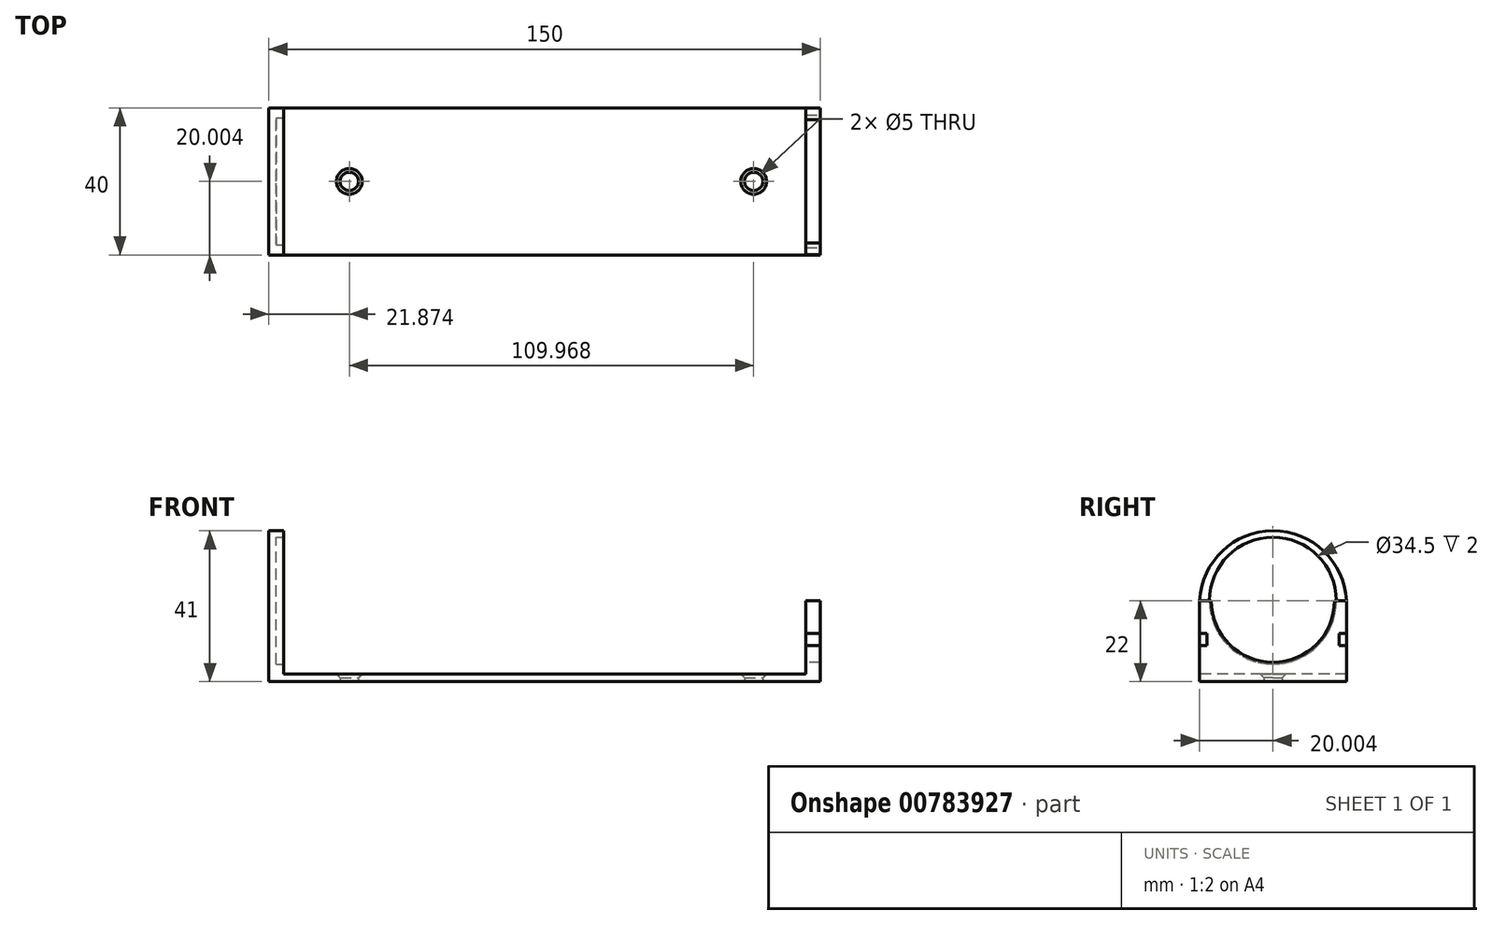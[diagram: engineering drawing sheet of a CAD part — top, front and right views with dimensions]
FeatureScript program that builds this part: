
annotation { "Feature Type Name" : "Feature", "Feature Type Description" : "" }
export const myFeature = defineFeature(function(context is Context, id is Id, definition is map)
    precondition{}
    {
        {
            var Q0;
            Q0=qCreatedBy(makeId("Top.planeOp"),FACE);
            var sketch = newSketch(context, id + "F0", { "sketchPlane" : qUnion([Q0])});
            skLineSegment(sketch, "E0.bottom", {"start": v(-45.04, -26.37) * mm, "end": v(104.96, -26.37) * mm});
            skLineSegment(sketch, "E0.top", {"start": v(-45.04, 13.63) * mm, "end": v(104.96, 13.63) * mm});
            skLineSegment(sketch, "E0.left", {"start": v(-45.04, -26.37) * mm, "end": v(-45.04, 13.63) * mm});
            skLineSegment(sketch, "E0.right", {"start": v(104.96, -26.37) * mm, "end": v(104.96, 13.63) * mm});
            skSolve(sketch);
        }
        {
            var Q0;
            Q0=makeQuery(id+"F0.imprint","IMPRINT",FACE,{"disambiguationData":[TD([[makeQuery(id+"F0.imprint","IMPRINT",EDGE,{"derivedFrom":sQuery(id+"F0.wireOp",EDGE,"E0.bottom")}),1.0]])]});
            extrude(context, id + "F1", {"entities" : qUnion([Q0]), "depth" : 2 * mm, "offsetDistance" : 25 * mm});
        }
        {
            var Q0;
            Q0=makeQuery(id+"F1.opExtrude","CAP_FACE",FACE,{"disambiguationData":[OSD([sQuery(id+"F0.wireOp",EDGE,"E0.bottom"),sQuery(id+"F0.wireOp",EDGE,"E0.top"),sQuery(id+"F0.wireOp",EDGE,"E0.left"),sQuery(id+"F0.wireOp",EDGE,"E0.right")])],"isStart":false});
            var sketch = newSketch(context, id + "F2", { "sketchPlane" : qUnion([Q0])});
            skLineSegment(sketch, "E1.bottom", {"start": v(-45.04, 13.63) * mm, "end": v(-41.04, 13.63) * mm});
            skLineSegment(sketch, "E1.top", {"start": v(-45.04, -26.37) * mm, "end": v(-41.04, -26.37) * mm});
            skLineSegment(sketch, "E1.left", {"start": v(-45.04, 13.63) * mm, "end": v(-45.04, -26.37) * mm});
            skLineSegment(sketch, "E1.right", {"start": v(-41.04, 13.63) * mm, "end": v(-41.04, -26.37) * mm});
            skLineSegment(sketch, "E2.bottom", {"start": v(104.96, 13.63) * mm, "end": v(102.96, 13.63) * mm});
            skLineSegment(sketch, "E2.top", {"start": v(104.96, -26.37) * mm, "end": v(102.96, -26.37) * mm});
            skLineSegment(sketch, "E2.left", {"start": v(104.96, 13.63) * mm, "end": v(104.96, -26.37) * mm});
            skLineSegment(sketch, "E2.right", {"start": v(102.96, 13.63) * mm, "end": v(102.96, -26.37) * mm});
            skSolve(sketch);
        }
        {
            var Q0;
            Q0=makeQuery(id+"F2.imprint","IMPRINT",FACE,{"disambiguationData":[TD([[makeQuery(id+"F2.imprint","IMPRINT",EDGE,{"derivedFrom":sQuery(id+"F2.wireOp",EDGE,"E1.bottom")}),-1.0]])]});
            var Q1;
            Q1=makeQuery(id+"F2.imprint","IMPRINT",FACE,{"disambiguationData":[TD([[makeQuery(id+"F2.imprint","IMPRINT",EDGE,{"derivedFrom":sQuery(id+"F2.wireOp",EDGE,"E2.bottom")}),-1.0]])]});
            extrude(context, id + "F3", {"entities" : qUnion([Q0, Q1]), "operationType" : NewBodyOperationType.ADD, "depth" : 40 * mm, "offsetDistance" : 25 * mm});
        }
        {
            var Q0;
            Q0=makeQuery(id+"F3.opExtrude","SWEPT_FACE",FACE,{"disambiguationData":[OSD([sQuery(id+"F2.wireOp",EDGE,"E1.right")])]});
            var sketch = newSketch(context, id + "F4", { "sketchPlane" : qUnion([Q0])});
            skCircle(sketch, "E3", {"center": v(-6.37, 22) * mm, "radius": 17.25 * mm});
            skSolve(sketch);
        }
        {
            var Q0;
            Q0=makeQuery(id+"F4.imprint","IMPRINT",FACE,{"disambiguationData":[TD([[makeQuery(id+"F4.imprint","IMPRINT",EDGE,{"derivedFrom":sQuery(id+"F4.wireOp",EDGE,"E3")}),1.0]])]});
            var Q1;
            Q1=sQuery(id+"F4.wireOp",EDGE,"E3");
            extrude(context, id + "F5", {"entities" : qUnion([Q0]), "operationType" : NewBodyOperationType.REMOVE, "surfaceEntities" : qUnion([Q1]), "oppositeDirection" : true, "depth" : 2 * mm, "offsetDistance" : 25 * mm});
        }
        {
            var Q0;
            Q0=makeQuery(id+"F3.opExtrude","SWEPT_FACE",FACE,{"disambiguationData":[OSD([sQuery(id+"F2.wireOp",EDGE,"E2.right")])]});
            var sketch = newSketch(context, id + "F6", { "sketchPlane" : qUnion([Q0])});
            skLineSegment(sketch, "E4", {"start": v(-10.38, 22) * mm, "end": v(23.12, 22) * mm});
            skArc(sketch, "E5", {"start": v(-10.38, 22) * mm, "mid": v(6.37, 5.25) * mm, "end": v(23.12, 22) * mm});
            skPoint(sketch, "E6.orphan", {"position": v(-13.63, 22) * mm});
            skPoint(sketch, "E7.orphan", {"position": v(26.37, 22) * mm});
            skSolve(sketch);
        }
        {
            var Q0;
            Q0=makeQuery(id+"F3.opExtrude","CAP_FACE",FACE,{"disambiguationData":[OSD([sQuery(id+"F2.wireOp",EDGE,"E2.bottom"),sQuery(id+"F2.wireOp",EDGE,"E2.top"),sQuery(id+"F2.wireOp",EDGE,"E2.left"),sQuery(id+"F2.wireOp",EDGE,"E2.right")])],"isStart":false});
            extrude(context, id + "F7", {"entities" : qUnion([Q0]), "operationType" : NewBodyOperationType.REMOVE, "oppositeDirection" : true, "depth" : 20 * mm, "offsetDistance" : 25 * mm});
        }
        {
            var Q0;
            Q0=makeQuery(id+"F6.imprint","IMPRINT",FACE,{"disambiguationData":[TD([[makeQuery(id+"F6.imprint","IMPRINT",EDGE,{"derivedFrom":sQuery(id+"F6.wireOp",EDGE,"E4")}),-1.0]])]});
            extrude(context, id + "F8", {"entities" : qUnion([Q0]), "operationType" : NewBodyOperationType.REMOVE, "endBound" : BoundingType.THROUGH_ALL, "oppositeDirection" : true, "depth" : 25 * mm, "offsetDistance" : 25 * mm});
        }
        {
            var Q0;
            Q0=makeQuery(id+"F1.opExtrude","CAP_FACE",FACE,{"disambiguationData":[OSD([sQuery(id+"F0.wireOp",EDGE,"E0.bottom"),sQuery(id+"F0.wireOp",EDGE,"E0.top"),sQuery(id+"F0.wireOp",EDGE,"E0.left"),sQuery(id+"F0.wireOp",EDGE,"E0.right")])],"isStart":true});
            var sketch = newSketch(context, id + "F9", { "sketchPlane" : qUnion([Q0])});
            skCircle(sketch, "E8", {"center": v(86.8, 6.37) * mm, "radius": 2.5 * mm});
            skCircle(sketch, "E9", {"center": v(-23.17, 6.37) * mm, "radius": 2.5 * mm});
            skSolve(sketch);
        }
        {
            var Q0;
            Q0=makeQuery(id+"F9.imprint","IMPRINT",FACE,{"disambiguationData":[TD([[makeQuery(id+"F9.imprint","IMPRINT",EDGE,{"derivedFrom":sQuery(id+"F9.wireOp",EDGE,"E9")}),1.0]])]});
            var Q1;
            Q1=makeQuery(id+"F9.imprint","IMPRINT",FACE,{"disambiguationData":[TD([[makeQuery(id+"F9.imprint","IMPRINT",EDGE,{"derivedFrom":sQuery(id+"F9.wireOp",EDGE,"E8")}),1.0]])]});
            extrude(context, id + "F10", {"entities" : qUnion([Q0, Q1]), "operationType" : NewBodyOperationType.REMOVE, "endBound" : BoundingType.THROUGH_ALL, "oppositeDirection" : true, "depth" : 25 * mm, "offsetDistance" : 25 * mm});
        }
        {
            var Q0;
            Q0=makeQuery(id+"F3.boolean.opBoolean","MERGE",FACE,{"derivedFrom":[makeQuery(id+"F1.opExtrude","SWEPT_FACE",FACE,{"disambiguationData":[OSD([sQuery(id+"F0.wireOp",EDGE,"E0.right")])]}),makeQuery(id+"F3.opExtrude","SWEPT_FACE",FACE,{"disambiguationData":[OSD([sQuery(id+"F2.wireOp",EDGE,"E2.left")])]})]});
            var sketch = newSketch(context, id + "F11", { "sketchPlane" : qUnion([Q0])});
            skLineSegment(sketch, "E10", {"start": v(-26.37, 13.12) * mm, "end": v(-24.37, 13.12) * mm});
            skLineSegment(sketch, "E11", {"start": v(-26.37, 9.8) * mm, "end": v(-24.37, 9.8) * mm});
            skLineSegment(sketch, "E12.0", {"start": v(-24.37, 13.12) * mm, "end": v(-24.37, 9.8) * mm});
            skLineSegment(sketch, "E13.0", {"start": v(11.63, 13.12) * mm, "end": v(11.63, 9.8) * mm});
            skLineSegment(sketch, "E14.trimOffspring", {"start": v(11.63, 13.12) * mm, "end": v(13.63, 13.12) * mm});
            skLineSegment(sketch, "E15.trimOffspring", {"start": v(11.63, 9.8) * mm, "end": v(13.63, 9.8) * mm});
            skSolve(sketch);
        }
        {
            var Q0;
            {var subQ0=sQuery(id+"F11.wireOp",EDGE,"E10");Q0=makeQuery(id+"F11.imprint","IMPRINT",FACE,{"disambiguationData":[TD([[makeQuery(id+"F11.imprint","IMPRINT",EDGE,{"derivedFrom":subQ0}),-1.0]])]});}
            var Q1;
            Q1=makeQuery(id+"F11.imprint","IMPRINT",FACE,{"disambiguationData":[TD([[makeQuery(id+"F11.imprint","IMPRINT",EDGE,{"derivedFrom":sQuery(id+"F11.wireOp",EDGE,"E13.0")}),1.0]])]});
            extrude(context, id + "F12", {"entities" : qUnion([Q0, Q1]), "operationType" : NewBodyOperationType.REMOVE, "oppositeDirection" : true, "depth" : 25 * mm, "offsetDistance" : 25 * mm});
        }
        {
            var Q0;
            Q0=makeQuery(id+"F3.boolean.opBoolean","MERGE",FACE,{"derivedFrom":[makeQuery(id+"F1.opExtrude","SWEPT_FACE",FACE,{"disambiguationData":[OSD([sQuery(id+"F0.wireOp",EDGE,"E0.left")])]}),makeQuery(id+"F3.opExtrude","SWEPT_FACE",FACE,{"disambiguationData":[OSD([sQuery(id+"F2.wireOp",EDGE,"E1.left")])]})]});
            var sketch = newSketch(context, id + "F13", { "sketchPlane" : qUnion([Q0])});
            skCircle(sketch, "E16", {"center": v(6.37, 21) * mm, "radius": 20 * mm});
            skPoint(sketch, "E16.centerSnap0", {"position": v(-13.63, 21) * mm});
            skPoint(sketch, "E16.centerSnap1", {"position": v(6.37, 42) * mm});
            skSolve(sketch);
        }
        {
            var Q0;
            {var subQ1=sQuery(id+"F2.wireOp",EDGE,"E1.left");var subQ7=makeQuery(id+"F3.opExtrude","CAP_EDGE",EDGE,{"disambiguationData":[OSD([subQ1])],"isStart":false});Q0=makeQuery(id+"F13.imprint","IMPRINT",FACE,{"disambiguationData":[TD([[makeQuery(id+"F13.imprint","IMPRINT",EDGE,{"derivedFrom":subQ7}),1.0]])]});}
            extrude(context, id + "F14", {"entities" : qUnion([Q0]), "operationType" : NewBodyOperationType.REMOVE, "endBound" : BoundingType.THROUGH_ALL, "oppositeDirection" : true, "depth" : 25 * mm, "offsetDistance" : 25 * mm});
        }
        {
            var Q0;
            Q0=makeQuery(id+"F10.boolean.opBoolean","INTERSECT",EDGE,{"derivedFrom":[makeQuery(id+"F1.opExtrude","CAP_FACE",FACE,{"disambiguationData":[OSD([sQuery(id+"F0.wireOp",EDGE,"E0.bottom"),sQuery(id+"F0.wireOp",EDGE,"E0.top"),sQuery(id+"F0.wireOp",EDGE,"E0.left"),sQuery(id+"F0.wireOp",EDGE,"E0.right")])],"isStart":false}),makeQuery(id+"F10.opExtrude","SWEPT_FACE",FACE,{"disambiguationData":[OSD([sQuery(id+"F9.wireOp",EDGE,"E9")])]})]});
            var Q1;
            Q1=makeQuery(id+"F10.boolean.opBoolean","INTERSECT",EDGE,{"derivedFrom":[makeQuery(id+"F1.opExtrude","CAP_FACE",FACE,{"disambiguationData":[OSD([sQuery(id+"F0.wireOp",EDGE,"E0.bottom"),sQuery(id+"F0.wireOp",EDGE,"E0.top"),sQuery(id+"F0.wireOp",EDGE,"E0.left"),sQuery(id+"F0.wireOp",EDGE,"E0.right")])],"isStart":false}),makeQuery(id+"F10.opExtrude","SWEPT_FACE",FACE,{"disambiguationData":[OSD([sQuery(id+"F9.wireOp",EDGE,"E8")])]})]});
            chamfer(context, id + "F15", {"entities" : qUnion([Q0, Q1]), "width" : 1 * mm, "tangentPropagation" : true});
        }
        {
            var Q0;
            Q0=makeQuery(id+"F3.opExtrude","SWEPT_FACE",FACE,{"disambiguationData":[OSD([sQuery(id+"F2.wireOp",EDGE,"E2.right")])]});
            extrude(context, id + "F16", {"entities" : qUnion([Q0]), "operationType" : NewBodyOperationType.ADD, "depth" : 2 * mm, "offsetDistance" : 25 * mm});
        }
    });
